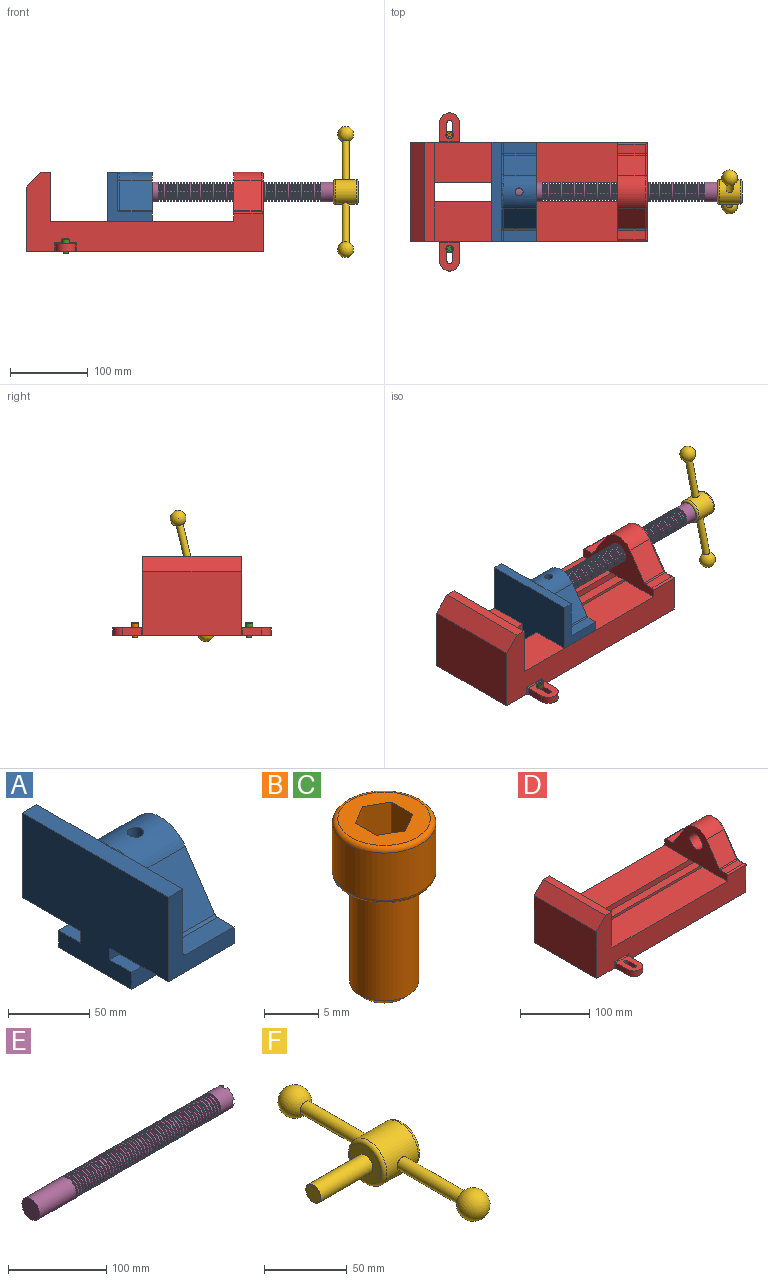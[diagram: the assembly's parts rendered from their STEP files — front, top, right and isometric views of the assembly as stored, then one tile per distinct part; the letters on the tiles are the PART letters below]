
ASSEMBLY  parts=6 mates=6
PART A: 36 faces, bbox 57.2x127x89 mm
  f0: plane 57.15x50.8mm, normal (0,0,-1), area 2903.2mm2, adj f6,f9,f10,f23
  f1: cylinder r=12.7mm len=44.45mm, axis (1,0,0), area 3464.3mm2, adj f6,f15,f16
  f2: plane 41.91x14.52mm, normal (0,0,1), area 608.5mm2, adj f6,f11,f24,f25
  f3: plane 51.86x48.26mm, normal (1,0,0), area 1495.7mm2, adj f8,f10,f31,f33,f35
  f4: plane 51.86x48.26mm, normal (1,0,0), area 1495.7mm2, adj f8,f11,f24,f28,f29
  f5: plane 57.15x50.8mm, normal (0,0,-1), area 2903.2mm2, adj f6,f9,f11,f22
  f6: plane 127x85.09mm, normal (1,0,0), area 5190.6mm2, adj f0,f1,f2,f5,f7,f10,f11,f12
  f7: plane 41.91x14.52mm, normal (0,0,1), area 608.5mm2, adj f6,f10,f30,f31
  f8: plane 127x12.7mm, normal (0,0,1), area 1612.9mm2, adj f3,f4,f9,f10,f11,f26,f34
  f9: plane 127x85.09mm, normal (-1,0,0), area 9096.8mm2, adj f0,f5,f8,f10,f11,f17,f18,f19
  f10: plane 63.5x57.15mm, normal (0,-1,0), area 1372.3mm2, adj f0,f3,f6,f7,f8,f9,f31
  f11: plane 63.5x57.15mm, normal (0,1,0), area 1372.3mm2, adj f2,f4,f5,f6,f8,f9,f24
  f12: plane 41.91x38.43mm, normal (0,-0.83,0.56), area 1939.2mm2, adj f6,f13,f30,f33
  f13: cylinder r=25.4mm len=44.45mm, axis (1,0,0), area 2026.5mm2, adj f6,f12,f14,f16,f26,f28,f34,f35
  f14: plane 41.91x38.43mm, normal (0,0.83,0.56), area 1939.2mm2, adj f6,f13,f25,f29
  f15: plane 25.4x25.4mm, normal (1,0,0), area 506.7mm2, adj f1
  f16: cylinder r=5.08mm len=13.76mm, axis (0,0,1), area 414mm2, adj f1,f13
  f17: plane 57.15x19.05mm, normal (0,0,1), area 1088.7mm2, adj f6,f9,f18,f23
  f18: plane 57.15x12.7mm, normal (0,-1,0), area 725.8mm2, adj f6,f9,f17,f19
  f19: plane 63.5x57.15mm, normal (0,0,-1), area 3629mm2, adj f6,f9,f18,f20
  f20: plane 57.15x12.7mm, normal (0,1,0), area 725.8mm2, adj f6,f9,f19,f21
  f21: plane 57.15x19.05mm, normal (0,0,1), area 1088.7mm2, adj f6,f9,f20,f22
  f22: plane 57.15x8.89mm, normal (0,1,0), area 508.1mm2, adj f5,f6,f9,f21
  f23: plane 57.15x8.89mm, normal (0,-1,0), area 508.1mm2, adj f0,f6,f9,f17
  f24: cylinder r=2.54mm len=14.52mm, axis (0,-1,0), area 57.9mm2, adj f2,f4,f11,f27
  f25: cylinder r=2.54mm len=41.91mm, axis (1,0,0), area 104.3mm2, adj f2,f6,f14,f27
  f26: bspline ~12.24x2.8mm, area 20.9mm2, adj f8,f13,f28
  f27: sphere r=2.54mm, area 6.3mm2, adj f24,f25,f29
  f28: torus R=27.94mm, axis (1,0,0), area 57.8mm2, adj f4,f13,f26,f29
  f29: cylinder r=2.54mm len=39.84mm, axis (0,-0.56,0.83), area 184.6mm2, adj f4,f14,f27,f28
  f30: cylinder r=2.54mm len=41.91mm, axis (1,0,0), area 104.3mm2, adj f6,f7,f12,f32
  f31: cylinder r=2.54mm len=14.52mm, axis (0,-1,0), area 57.9mm2, adj f3,f7,f10,f32
  f32: sphere r=2.54mm, area 6.3mm2, adj f30,f31,f33
  f33: cylinder r=2.54mm len=39.84mm, axis (0,-0.56,-0.83), area 184.6mm2, adj f3,f12,f32,f35
  f34: bspline ~12.24x2.8mm, area 20.9mm2, adj f8,f13,f35
  f35: torus R=27.94mm, axis (1,0,0), area 57.8mm2, adj f3,f13,f33,f34
PART B: 15 faces, bbox 10.3x10.3x19.1 mm
  f0: plane 8.51x8.51mm, normal (0,0,1), area 37.2mm2, adj f5,f6,f7,f8,f9,f10,f14
  f1: cylinder r=3.17mm len=11.94mm, axis (0,0,1), area 238.2mm2, adj f4,f12
  f2: plane 4.83x4.83mm, normal (0,0,-1), area 18.3mm2, adj f12
  f3: cylinder r=4.76mm len=9.53mm, axis (0,0,-1), area 159.6mm2, adj f13,f14
  f4: plane 8.51x8.51mm, normal (0,0,-1), area 25.2mm2, adj f1,f13
  f5: plane 4.83x2.38mm, normal (-0.5,-0.87,0), area 13.3mm2, adj f0,f6,f10,f11
  f6: plane 4.83x2.38mm, normal (0.5,-0.87,0), area 13.3mm2, adj f0,f5,f7,f11
  f7: plane 4.83x2.75mm, normal (1,0,0), area 13.3mm2, adj f0,f6,f8,f11
  f8: plane 4.83x2.38mm, normal (0.5,0.87,0), area 13.3mm2, adj f0,f7,f9,f11
  f9: plane 4.83x2.38mm, normal (-0.5,0.87,0), area 13.3mm2, adj f0,f8,f10,f11
  f10: plane 4.83x2.75mm, normal (-1,0,0), area 13.3mm2, adj f0,f5,f9,f11
  f11: plane 5.5x4.76mm, normal (0,0,1), area 19.6mm2, adj f5,f6,f7,f8,f9,f10
  f12: cone r=3.17mm half-angle=45deg, axis (0,0,1), area 18.9mm2, adj f1,f2
  f13: torus R=4.25mm, axis (0,0,1), area 23mm2, adj f3,f4
  f14: torus R=4.25mm, axis (0,0,1), area 23mm2, adj f0,f3
PART C: same geometry as B
PART D: 61 faces, bbox 304.8x203.2x103.7 mm
  f0: plane 304.8x101.6mm, normal (0,1,0), area 13520.3mm2, adj f3,f4,f5,f6,f7,f8,f9,f16
  f1: plane 304.8x101.6mm, normal (0,-1,0), area 13520.3mm2, adj f2,f3,f5,f6,f7,f8,f9,f16
  f2: plane 234.95x50.8mm, normal (0,0,1), area 11935.5mm2, adj f1,f5,f16,f26
  f3: plane 127x99.06mm, normal (1,0,0), area 7097.5mm2, adj f0,f1,f9,f14,f17,f18,f19,f20
  f4: plane 234.95x50.8mm, normal (0,0,1), area 11935.5mm2, adj f0,f5,f16,f27
  f5: plane 127x101.6mm, normal (1,0,0), area 9516.1mm2, adj f0,f1,f2,f4,f6,f9,f18,f19
  f6: plane 127x12.7mm, normal (0,0,1), area 1612.9mm2, adj f0,f1,f5,f7
  f7: plane 127x19.05mm, normal (-0.71,0,0.71), area 3421.5mm2, adj f0,f1,f6,f8
  f8: plane 127x82.55mm, normal (-1,0,0), area 10483.8mm2, adj f0,f1,f7,f9
  f9: plane 304.8x203.2mm, normal (0,0,-1), area 33298.3mm2, adj f0,f1,f3,f5,f8,f21,f22,f39
  f10: plane 35.56x11.98mm, normal (0,0,1), area 426mm2, adj f16,f28,f29,f30
  f11: plane 38.43x35.56mm, normal (0,0.83,0.56), area 1645.4mm2, adj f12,f16,f29,f32
  f12: cylinder r=25.4mm len=42.19mm, axis (1,0,0), area 1770.2mm2, adj f11,f13,f16,f33
  f13: plane 38.43x35.56mm, normal (0,-0.83,0.56), area 1645.4mm2, adj f12,f16,f34,f35
  f14: cylinder r=12.7mm len=38.1mm, axis (1,0,0), area 3040.2mm2, adj f3,f16
  f15: plane 35.56x11.98mm, normal (0,0,1), area 426mm2, adj f16,f34,f36,f38
  f16: plane 127x63.5mm, normal (-1,0,0), area 4155.5mm2, adj f0,f1,f2,f4,f10,f11,f12,f13
  f17: plane 38.1x25.4mm, normal (0,0,-1), area 967.7mm2, adj f3,f16,f26,f27
  f18: plane 273.05x19.05mm, normal (0,0,-1), area 5201.6mm2, adj f3,f5,f19,f26
  f19: plane 273.05x12.7mm, normal (0,1,0), area 3467.7mm2, adj f3,f5,f18,f20
  f20: plane 273.05x19.05mm, normal (0,0,1), area 5201.6mm2, adj f3,f5,f19,f21
  f21: plane 273.05x16.51mm, normal (0,1,0), area 4508.1mm2, adj f3,f5,f9,f20
  f22: plane 273.05x16.51mm, normal (0,-1,0), area 4508.1mm2, adj f3,f5,f9,f23
  f23: plane 273.05x19.05mm, normal (0,0,1), area 5201.6mm2, adj f3,f5,f22,f24
  f24: plane 273.05x12.7mm, normal (0,-1,0), area 3467.7mm2, adj f3,f5,f23,f25
  f25: plane 273.05x19.05mm, normal (0,0,-1), area 5201.6mm2, adj f3,f5,f24,f27
  f26: plane 273.05x8.89mm, normal (0,1,0), area 2427.4mm2, adj f2,f3,f5,f17,f18
  f27: plane 273.05x8.89mm, normal (0,-1,0), area 2427.4mm2, adj f3,f4,f5,f17,f25
  f28: cylinder r=2.54mm len=38.1mm, axis (1,0,0), area 148.3mm2, adj f0,f10,f16,f30
  f29: cylinder r=2.54mm len=35.56mm, axis (-1,0,0), area 88.5mm2, adj f10,f11,f16,f31
  f30: cylinder r=2.54mm len=14.52mm, axis (0,1,0), area 54.3mm2, adj f3,f10,f28,f31
  f31: torus R=5.08mm, axis (-1,0,0), area 13.5mm2, adj f3,f29,f30,f32
  f32: cylinder r=2.54mm len=39.84mm, axis (0,0.56,-0.83), area 184.6mm2, adj f3,f11,f31,f33
  f33: torus R=22.86mm, axis (-1,0,0), area 191.4mm2, adj f3,f12,f32,f35
  f34: cylinder r=2.54mm len=35.56mm, axis (-1,0,0), area 88.5mm2, adj f13,f15,f16,f37
  f35: cylinder r=2.54mm len=39.84mm, axis (0,0.56,0.83), area 184.6mm2, adj f3,f13,f33,f37
  f36: cylinder r=2.54mm len=38.1mm, axis (-1,0,0), area 148.3mm2, adj f1,f15,f16,f38
  f37: torus R=5.08mm, axis (-1,0,0), area 13.5mm2, adj f3,f34,f35,f38
  f38: cylinder r=2.54mm len=14.52mm, axis (0,1,0), area 54.3mm2, adj f3,f15,f36,f37
  f39: plane 23.88x9.53mm, normal (-1,0,0), area 227.4mm2, adj f9,f45,f46,f60
  f40: plane 23.88x9.53mm, normal (1,0,0), area 227.4mm2, adj f9,f45,f46,f58
  f41: cylinder r=3.3mm len=9.53mm, axis (0,0,-1), area 98.8mm2, adj f9,f42,f44,f46
  f42: plane 15.62x9.53mm, normal (-1,0,0), area 148.8mm2, adj f9,f41,f43,f46
  f43: cylinder r=3.3mm len=9.53mm, axis (0,0,-1), area 98.8mm2, adj f9,f42,f44,f46
  f44: plane 15.62x9.53mm, normal (1,0,0), area 148.8mm2, adj f9,f41,f43,f46
  f45: cylinder r=12.7mm len=25.4mm, axis (0,0,-1), area 380mm2, adj f9,f39,f40,f46
  f46: plane 36.58x25.4mm, normal (0,0,1), area 722.4mm2, adj f39,f40,f41,f42,f43,f44,f45,f59
  f47: plane 23.88x9.53mm, normal (-1,0,0), area 227.4mm2, adj f9,f53,f54,f56
  f48: plane 23.88x9.53mm, normal (1,0,0), area 227.4mm2, adj f9,f53,f54,f55
  f49: cylinder r=3.3mm len=9.53mm, axis (0,0,-1), area 98.8mm2, adj f9,f50,f52,f54
  f50: plane 15.62x9.53mm, normal (-1,0,0), area 148.8mm2, adj f9,f49,f51,f54
  f51: cylinder r=3.3mm len=9.53mm, axis (0,0,-1), area 98.8mm2, adj f9,f50,f52,f54
  f52: plane 15.62x9.53mm, normal (1,0,0), area 148.8mm2, adj f9,f49,f51,f54
  f53: cylinder r=12.7mm len=25.4mm, axis (0,0,-1), area 380mm2, adj f9,f47,f48,f54
  f54: plane 36.58x25.4mm, normal (0,0,1), area 722.4mm2, adj f47,f48,f49,f50,f51,f52,f53,f57
  f55: cylinder r=1.52mm len=11.05mm, axis (0,0,-1), area 24.1mm2, adj f0,f9,f48,f57
  f56: cylinder r=1.52mm len=11.05mm, axis (0,0,1), area 24.1mm2, adj f0,f9,f47,f57
  f57: cylinder r=1.52mm len=28.45mm, axis (1,0,0), area 63.5mm2, adj f0,f54,f55,f56
  f58: cylinder r=1.52mm len=11.05mm, axis (0,0,1), area 24.1mm2, adj f1,f9,f40,f59
  f59: cylinder r=1.52mm len=28.45mm, axis (-1,0,0), area 63.5mm2, adj f1,f46,f58,f60
  f60: cylinder r=1.52mm len=11.05mm, axis (0,0,-1), area 24.1mm2, adj f1,f9,f39,f59
PART E: 220 faces, bbox 279.4x25.4x25.4 mm
  f0: cylinder r=12.7mm len=25.4mm, axis (-1,0,0), area 1468.2mm2, adj f1,f2,f3,f5,f7,f208,f209,f210
  f1: plane 9.9x9.9mm, normal (1,0,0), area 62.3mm2, adj f0,f4,f213,f216
  f2: plane 9.9x9.9mm, normal (1,0,0), area 62.3mm2, adj f0,f4,f210,f218
  f3: plane 9.9x9.9mm, normal (1,0,0), area 62.3mm2, adj f0,f4,f209,f212
  f4: cylinder r=6.35mm len=25.4mm, axis (1,0,0), area 960.3mm2, adj f1,f2,f3,f5,f6,f208,f209,f210
  f5: plane 9.9x9.9mm, normal (1,0,0), area 62.3mm2, adj f0,f4,f215,f217
  f6: plane 12.7x12.7mm, normal (1,0,0), area 126.7mm2, adj f4
  f7: cone r=12.7mm half-angle=76deg, axis (1,0,0), area 188mm2, adj f0,f9
  f8: cone r=10.16mm half-angle=76deg, axis (-1,0,0), area 188mm2, adj f9,f10
  f9: cylinder r=10.16mm len=20.32mm, axis (1,0,0), area 81.1mm2, adj f7,f8
  f10: cylinder r=12.7mm len=25.4mm, axis (-1,0,0), area 131.7mm2, adj f8,f11
  f11: cone r=12.7mm half-angle=76deg, axis (1,0,0), area 188mm2, adj f10,f13
  f12: cone r=10.16mm half-angle=76deg, axis (-1,0,0), area 188mm2, adj f13,f14
  f13: cylinder r=10.16mm len=20.32mm, axis (1,0,0), area 81.1mm2, adj f11,f12
  f14: cylinder r=12.7mm len=25.4mm, axis (-1,0,0), area 131.7mm2, adj f12,f15
  f15: cone r=12.7mm half-angle=76deg, axis (1,0,0), area 188mm2, adj f14,f17
  f16: cone r=10.16mm half-angle=76deg, axis (-1,0,0), area 188mm2, adj f17,f18
  f17: cylinder r=10.16mm len=20.32mm, axis (1,0,0), area 81.1mm2, adj f15,f16
  f18: cylinder r=12.7mm len=25.4mm, axis (-1,0,0), area 131.7mm2, adj f16,f19
  f19: cone r=12.7mm half-angle=76deg, axis (1,0,0), area 188mm2, adj f18,f21
  f20: cone r=10.16mm half-angle=76deg, axis (-1,0,0), area 188mm2, adj f21,f22
  f21: cylinder r=10.16mm len=20.32mm, axis (1,0,0), area 81.1mm2, adj f19,f20
  f22: cylinder r=12.7mm len=25.4mm, axis (-1,0,0), area 131.7mm2, adj f20,f23
  f23: cone r=12.7mm half-angle=76deg, axis (1,0,0), area 188mm2, adj f22,f25
  f24: cone r=10.16mm half-angle=76deg, axis (-1,0,0), area 188mm2, adj f25,f26
  f25: cylinder r=10.16mm len=20.32mm, axis (1,0,0), area 81.1mm2, adj f23,f24
  f26: cylinder r=12.7mm len=25.4mm, axis (-1,0,0), area 131.7mm2, adj f24,f27
  f27: cone r=12.7mm half-angle=76deg, axis (1,0,0), area 188mm2, adj f26,f29
  f28: cone r=10.16mm half-angle=76deg, axis (-1,0,0), area 188mm2, adj f29,f30
  f29: cylinder r=10.16mm len=20.32mm, axis (1,0,0), area 81.1mm2, adj f27,f28
  f30: cylinder r=12.7mm len=25.4mm, axis (-1,0,0), area 131.7mm2, adj f28,f31
  f31: cone r=12.7mm half-angle=76deg, axis (1,0,0), area 188mm2, adj f30,f33
  f32: cone r=10.16mm half-angle=76deg, axis (-1,0,0), area 188mm2, adj f33,f34
  f33: cylinder r=10.16mm len=20.32mm, axis (1,0,0), area 81.1mm2, adj f31,f32
  f34: cylinder r=12.7mm len=25.4mm, axis (-1,0,0), area 131.7mm2, adj f32,f35
  f35: cone r=12.7mm half-angle=76deg, axis (1,0,0), area 188mm2, adj f34,f37
  f36: cone r=10.16mm half-angle=76deg, axis (-1,0,0), area 188mm2, adj f37,f38
  f37: cylinder r=10.16mm len=20.32mm, axis (1,0,0), area 81.1mm2, adj f35,f36
  f38: cylinder r=12.7mm len=25.4mm, axis (-1,0,0), area 131.7mm2, adj f36,f39
  f39: cone r=12.7mm half-angle=76deg, axis (1,0,0), area 188mm2, adj f38,f41
  f40: cone r=10.16mm half-angle=76deg, axis (-1,0,0), area 188mm2, adj f41,f42
  f41: cylinder r=10.16mm len=20.32mm, axis (1,0,0), area 81.1mm2, adj f39,f40
  f42: cylinder r=12.7mm len=25.4mm, axis (-1,0,0), area 131.7mm2, adj f40,f43
  f43: cone r=12.7mm half-angle=76deg, axis (1,0,0), area 188mm2, adj f42,f45
  f44: cone r=10.16mm half-angle=76deg, axis (-1,0,0), area 188mm2, adj f45,f46
  f45: cylinder r=10.16mm len=20.32mm, axis (1,0,0), area 81.1mm2, adj f43,f44
  f46: cylinder r=12.7mm len=25.4mm, axis (-1,0,0), area 131.7mm2, adj f44,f47
  f47: cone r=12.7mm half-angle=76deg, axis (1,0,0), area 188mm2, adj f46,f49
  f48: cone r=10.16mm half-angle=76deg, axis (-1,0,0), area 188mm2, adj f49,f50
  f49: cylinder r=10.16mm len=20.32mm, axis (1,0,0), area 81.1mm2, adj f47,f48
  f50: cylinder r=12.7mm len=25.4mm, axis (-1,0,0), area 131.7mm2, adj f48,f51
  f51: cone r=12.7mm half-angle=76deg, axis (1,0,0), area 188mm2, adj f50,f53
  f52: cone r=10.16mm half-angle=76deg, axis (-1,0,0), area 188mm2, adj f53,f54
  f53: cylinder r=10.16mm len=20.32mm, axis (1,0,0), area 81.1mm2, adj f51,f52
  f54: cylinder r=12.7mm len=25.4mm, axis (-1,0,0), area 131.7mm2, adj f52,f55
  f55: cone r=12.7mm half-angle=76deg, axis (1,0,0), area 188mm2, adj f54,f57
  f56: cone r=10.16mm half-angle=76deg, axis (-1,0,0), area 188mm2, adj f57,f58
  f57: cylinder r=10.16mm len=20.32mm, axis (1,0,0), area 81.1mm2, adj f55,f56
  f58: cylinder r=12.7mm len=25.4mm, axis (-1,0,0), area 131.7mm2, adj f56,f59
  f59: cone r=12.7mm half-angle=76deg, axis (1,0,0), area 188mm2, adj f58,f61
  f60: cone r=10.16mm half-angle=76deg, axis (-1,0,0), area 188mm2, adj f61,f62
  f61: cylinder r=10.16mm len=20.32mm, axis (1,0,0), area 81.1mm2, adj f59,f60
  f62: cylinder r=12.7mm len=25.4mm, axis (-1,0,0), area 131.7mm2, adj f60,f63
  f63: cone r=12.7mm half-angle=76deg, axis (1,0,0), area 188mm2, adj f62,f65
  f64: cone r=10.16mm half-angle=76deg, axis (-1,0,0), area 188mm2, adj f65,f66
  f65: cylinder r=10.16mm len=20.32mm, axis (1,0,0), area 81.1mm2, adj f63,f64
  f66: cylinder r=12.7mm len=25.4mm, axis (-1,0,0), area 131.7mm2, adj f64,f67
  f67: cone r=12.7mm half-angle=76deg, axis (1,0,0), area 188mm2, adj f66,f69
  f68: cone r=10.16mm half-angle=76deg, axis (-1,0,0), area 188mm2, adj f69,f70
  f69: cylinder r=10.16mm len=20.32mm, axis (1,0,0), area 81.1mm2, adj f67,f68
  f70: cylinder r=12.7mm len=25.4mm, axis (-1,0,0), area 131.7mm2, adj f68,f71
  f71: cone r=12.7mm half-angle=76deg, axis (1,0,0), area 188mm2, adj f70,f73
  f72: cone r=10.16mm half-angle=76deg, axis (-1,0,0), area 188mm2, adj f73,f74
  f73: cylinder r=10.16mm len=20.32mm, axis (1,0,0), area 81.1mm2, adj f71,f72
  f74: cylinder r=12.7mm len=25.4mm, axis (-1,0,0), area 131.7mm2, adj f72,f75
  f75: cone r=12.7mm half-angle=76deg, axis (1,0,0), area 188mm2, adj f74,f77
  f76: cone r=10.16mm half-angle=76deg, axis (-1,0,0), area 188mm2, adj f77,f78
  f77: cylinder r=10.16mm len=20.32mm, axis (1,0,0), area 81.1mm2, adj f75,f76
  f78: cylinder r=12.7mm len=25.4mm, axis (-1,0,0), area 131.7mm2, adj f76,f79
  f79: cone r=12.7mm half-angle=76deg, axis (1,0,0), area 188mm2, adj f78,f81
  f80: cone r=10.16mm half-angle=76deg, axis (-1,0,0), area 188mm2, adj f81,f82
  f81: cylinder r=10.16mm len=20.32mm, axis (1,0,0), area 81.1mm2, adj f79,f80
  f82: cylinder r=12.7mm len=25.4mm, axis (-1,0,0), area 131.7mm2, adj f80,f83
  f83: cone r=12.7mm half-angle=76deg, axis (1,0,0), area 188mm2, adj f82,f85
  f84: cone r=10.16mm half-angle=76deg, axis (-1,0,0), area 188mm2, adj f85,f86
  f85: cylinder r=10.16mm len=20.32mm, axis (1,0,0), area 81.1mm2, adj f83,f84
  f86: cylinder r=12.7mm len=25.4mm, axis (-1,0,0), area 131.7mm2, adj f84,f87
  f87: cone r=12.7mm half-angle=76deg, axis (1,0,0), area 188mm2, adj f86,f89
  f88: cone r=10.16mm half-angle=76deg, axis (-1,0,0), area 188mm2, adj f89,f90
  f89: cylinder r=10.16mm len=20.32mm, axis (1,0,0), area 81.1mm2, adj f87,f88
  f90: cylinder r=12.7mm len=25.4mm, axis (-1,0,0), area 131.7mm2, adj f88,f91
  f91: cone r=12.7mm half-angle=76deg, axis (1,0,0), area 188mm2, adj f90,f93
  f92: cone r=10.16mm half-angle=76deg, axis (-1,0,0), area 188mm2, adj f93,f94
  f93: cylinder r=10.16mm len=20.32mm, axis (1,0,0), area 81.1mm2, adj f91,f92
  f94: cylinder r=12.7mm len=25.4mm, axis (-1,0,0), area 131.7mm2, adj f92,f95
  f95: cone r=12.7mm half-angle=76deg, axis (1,0,0), area 188mm2, adj f94,f97
  f96: cone r=10.16mm half-angle=76deg, axis (-1,0,0), area 188mm2, adj f97,f98
  f97: cylinder r=10.16mm len=20.32mm, axis (1,0,0), area 81.1mm2, adj f95,f96
  f98: cylinder r=12.7mm len=25.4mm, axis (-1,0,0), area 131.7mm2, adj f96,f99
  f99: cone r=12.7mm half-angle=76deg, axis (1,0,0), area 188mm2, adj f98,f101
  f100: cone r=10.16mm half-angle=76deg, axis (-1,0,0), area 188mm2, adj f101,f102
  f101: cylinder r=10.16mm len=20.32mm, axis (1,0,0), area 81.1mm2, adj f99,f100
  f102: cylinder r=12.7mm len=25.4mm, axis (-1,0,0), area 131.7mm2, adj f100,f103
  f103: cone r=12.7mm half-angle=76deg, axis (1,0,0), area 188mm2, adj f102,f105
  f104: cone r=10.16mm half-angle=76deg, axis (-1,0,0), area 188mm2, adj f105,f106
  f105: cylinder r=10.16mm len=20.32mm, axis (1,0,0), area 81.1mm2, adj f103,f104
  f106: cylinder r=12.7mm len=25.4mm, axis (-1,0,0), area 131.7mm2, adj f104,f107
  f107: cone r=12.7mm half-angle=76deg, axis (1,0,0), area 188mm2, adj f106,f109
  f108: cone r=10.16mm half-angle=76deg, axis (-1,0,0), area 188mm2, adj f109,f110
  f109: cylinder r=10.16mm len=20.32mm, axis (1,0,0), area 81.1mm2, adj f107,f108
  f110: cylinder r=12.7mm len=25.4mm, axis (-1,0,0), area 131.7mm2, adj f108,f111
  f111: cone r=12.7mm half-angle=76deg, axis (1,0,0), area 188mm2, adj f110,f113
  f112: cone r=10.16mm half-angle=76deg, axis (-1,0,0), area 188mm2, adj f113,f114
  f113: cylinder r=10.16mm len=20.32mm, axis (1,0,0), area 81.1mm2, adj f111,f112
  f114: cylinder r=12.7mm len=25.4mm, axis (-1,0,0), area 131.7mm2, adj f112,f115
  f115: cone r=12.7mm half-angle=76deg, axis (1,0,0), area 188mm2, adj f114,f117
  f116: cone r=10.16mm half-angle=76deg, axis (-1,0,0), area 188mm2, adj f117,f118
  f117: cylinder r=10.16mm len=20.32mm, axis (1,0,0), area 81.1mm2, adj f115,f116
  f118: cylinder r=12.7mm len=25.4mm, axis (-1,0,0), area 131.7mm2, adj f116,f119
  f119: cone r=12.7mm half-angle=76deg, axis (1,0,0), area 188mm2, adj f118,f121
  f120: cone r=10.16mm half-angle=76deg, axis (-1,0,0), area 188mm2, adj f121,f122
  f121: cylinder r=10.16mm len=20.32mm, axis (1,0,0), area 81.1mm2, adj f119,f120
  f122: cylinder r=12.7mm len=25.4mm, axis (-1,0,0), area 131.7mm2, adj f120,f123
  f123: cone r=12.7mm half-angle=76deg, axis (1,0,0), area 188mm2, adj f122,f125
  f124: cone r=10.16mm half-angle=76deg, axis (-1,0,0), area 188mm2, adj f125,f126
  f125: cylinder r=10.16mm len=20.32mm, axis (1,0,0), area 81.1mm2, adj f123,f124
  f126: cylinder r=12.7mm len=25.4mm, axis (-1,0,0), area 131.7mm2, adj f124,f127
  f127: cone r=12.7mm half-angle=76deg, axis (1,0,0), area 188mm2, adj f126,f129
  f128: cone r=10.16mm half-angle=76deg, axis (-1,0,0), area 188mm2, adj f129,f130
  f129: cylinder r=10.16mm len=20.32mm, axis (1,0,0), area 81.1mm2, adj f127,f128
  f130: cylinder r=12.7mm len=25.4mm, axis (-1,0,0), area 131.7mm2, adj f128,f131
  f131: cone r=12.7mm half-angle=76deg, axis (1,0,0), area 188mm2, adj f130,f133
  f132: cone r=10.16mm half-angle=76deg, axis (-1,0,0), area 188mm2, adj f133,f134
  f133: cylinder r=10.16mm len=20.32mm, axis (1,0,0), area 81.1mm2, adj f131,f132
  f134: cylinder r=12.7mm len=25.4mm, axis (-1,0,0), area 131.7mm2, adj f132,f135
  f135: cone r=12.7mm half-angle=76deg, axis (1,0,0), area 188mm2, adj f134,f137
  f136: cone r=10.16mm half-angle=76deg, axis (-1,0,0), area 188mm2, adj f137,f138
  f137: cylinder r=10.16mm len=20.32mm, axis (1,0,0), area 81.1mm2, adj f135,f136
  f138: cylinder r=12.7mm len=25.4mm, axis (-1,0,0), area 131.7mm2, adj f136,f139
  f139: cone r=12.7mm half-angle=76deg, axis (1,0,0), area 188mm2, adj f138,f141
  f140: cone r=10.16mm half-angle=76deg, axis (-1,0,0), area 188mm2, adj f141,f142
  f141: cylinder r=10.16mm len=20.32mm, axis (1,0,0), area 81.1mm2, adj f139,f140
  f142: cylinder r=12.7mm len=25.4mm, axis (-1,0,0), area 131.7mm2, adj f140,f143
  f143: cone r=12.7mm half-angle=76deg, axis (1,0,0), area 188mm2, adj f142,f145
  f144: cone r=10.16mm half-angle=76deg, axis (-1,0,0), area 188mm2, adj f145,f146
  f145: cylinder r=10.16mm len=20.32mm, axis (1,0,0), area 81.1mm2, adj f143,f144
  f146: cylinder r=12.7mm len=25.4mm, axis (-1,0,0), area 131.7mm2, adj f144,f147
  f147: cone r=12.7mm half-angle=76deg, axis (1,0,0), area 188mm2, adj f146,f149
  f148: cone r=10.16mm half-angle=76deg, axis (-1,0,0), area 188mm2, adj f149,f150
  f149: cylinder r=10.16mm len=20.32mm, axis (1,0,0), area 81.1mm2, adj f147,f148
  f150: cylinder r=12.7mm len=25.4mm, axis (-1,0,0), area 131.7mm2, adj f148,f151
  f151: cone r=12.7mm half-angle=76deg, axis (1,0,0), area 188mm2, adj f150,f153
  f152: cone r=10.16mm half-angle=76deg, axis (-1,0,0), area 188mm2, adj f153,f154
  f153: cylinder r=10.16mm len=20.32mm, axis (1,0,0), area 81.1mm2, adj f151,f152
  f154: cylinder r=12.7mm len=25.4mm, axis (-1,0,0), area 131.7mm2, adj f152,f155
  f155: cone r=12.7mm half-angle=76deg, axis (1,0,0), area 188mm2, adj f154,f157
  f156: cone r=10.16mm half-angle=76deg, axis (-1,0,0), area 188mm2, adj f157,f158
  f157: cylinder r=10.16mm len=20.32mm, axis (1,0,0), area 81.1mm2, adj f155,f156
  f158: cylinder r=12.7mm len=25.4mm, axis (-1,0,0), area 131.7mm2, adj f156,f159
  f159: cone r=12.7mm half-angle=76deg, axis (1,0,0), area 188mm2, adj f158,f161
  f160: cone r=10.16mm half-angle=76deg, axis (-1,0,0), area 188mm2, adj f161,f162
  f161: cylinder r=10.16mm len=20.32mm, axis (1,0,0), area 81.1mm2, adj f159,f160
  f162: cylinder r=12.7mm len=25.4mm, axis (-1,0,0), area 131.7mm2, adj f160,f163
  f163: cone r=12.7mm half-angle=76deg, axis (1,0,0), area 188mm2, adj f162,f165
  f164: cone r=10.16mm half-angle=76deg, axis (-1,0,0), area 188mm2, adj f165,f166
  f165: cylinder r=10.16mm len=20.32mm, axis (1,0,0), area 81.1mm2, adj f163,f164
  f166: cylinder r=12.7mm len=25.4mm, axis (-1,0,0), area 131.7mm2, adj f164,f167
  f167: cone r=12.7mm half-angle=76deg, axis (1,0,0), area 188mm2, adj f166,f169
  f168: cone r=10.16mm half-angle=76deg, axis (-1,0,0), area 188mm2, adj f169,f170
  f169: cylinder r=10.16mm len=20.32mm, axis (1,0,0), area 81.1mm2, adj f167,f168
  f170: cylinder r=12.7mm len=25.4mm, axis (-1,0,0), area 131.7mm2, adj f168,f171
  f171: cone r=12.7mm half-angle=76deg, axis (1,0,0), area 188mm2, adj f170,f173
  f172: cone r=10.16mm half-angle=76deg, axis (-1,0,0), area 188mm2, adj f173,f174
  f173: cylinder r=10.16mm len=20.32mm, axis (1,0,0), area 81.1mm2, adj f171,f172
  f174: cylinder r=12.7mm len=25.4mm, axis (-1,0,0), area 131.7mm2, adj f172,f175
  f175: cone r=12.7mm half-angle=76deg, axis (1,0,0), area 188mm2, adj f174,f177
  f176: cone r=10.16mm half-angle=76deg, axis (-1,0,0), area 188mm2, adj f177,f178
  f177: cylinder r=10.16mm len=20.32mm, axis (1,0,0), area 81.1mm2, adj f175,f176
  f178: cylinder r=12.7mm len=25.4mm, axis (-1,0,0), area 131.7mm2, adj f176,f179
  f179: cone r=12.7mm half-angle=76deg, axis (1,0,0), area 188mm2, adj f178,f181
  f180: cone r=10.16mm half-angle=76deg, axis (-1,0,0), area 188mm2, adj f181,f182
  f181: cylinder r=10.16mm len=20.32mm, axis (1,0,0), area 81.1mm2, adj f179,f180
  f182: cylinder r=12.7mm len=25.4mm, axis (-1,0,0), area 131.7mm2, adj f180,f183
  f183: cone r=12.7mm half-angle=76deg, axis (1,0,0), area 188mm2, adj f182,f185
  f184: cone r=10.16mm half-angle=76deg, axis (-1,0,0), area 188mm2, adj f185,f186
  f185: cylinder r=10.16mm len=20.32mm, axis (1,0,0), area 81.1mm2, adj f183,f184
  f186: cylinder r=12.7mm len=25.4mm, axis (-1,0,0), area 131.7mm2, adj f184,f187
  f187: cone r=12.7mm half-angle=76deg, axis (1,0,0), area 188mm2, adj f186,f189
  f188: cone r=10.16mm half-angle=76deg, axis (-1,0,0), area 188mm2, adj f189,f190
  f189: cylinder r=10.16mm len=20.32mm, axis (1,0,0), area 81.1mm2, adj f187,f188
  f190: cylinder r=12.7mm len=25.4mm, axis (-1,0,0), area 131.7mm2, adj f188,f191
  f191: cone r=12.7mm half-angle=76deg, axis (1,0,0), area 188mm2, adj f190,f193
  f192: cone r=10.16mm half-angle=76deg, axis (-1,0,0), area 188mm2, adj f193,f194
  f193: cylinder r=10.16mm len=20.32mm, axis (1,0,0), area 81.1mm2, adj f191,f192
  f194: cylinder r=12.7mm len=25.4mm, axis (-1,0,0), area 131.7mm2, adj f192,f195
  f195: cone r=12.7mm half-angle=76deg, axis (1,0,0), area 188mm2, adj f194,f197
  f196: cone r=10.16mm half-angle=76deg, axis (-1,0,0), area 188mm2, adj f197,f198
  f197: cylinder r=10.16mm len=20.32mm, axis (1,0,0), area 81.1mm2, adj f195,f196
  f198: cylinder r=12.7mm len=25.4mm, axis (-1,0,0), area 131.7mm2, adj f196,f199
  f199: cone r=12.7mm half-angle=76deg, axis (1,0,0), area 188mm2, adj f198,f201
  f200: cone r=10.16mm half-angle=76deg, axis (-1,0,0), area 188mm2, adj f201,f202
  f201: cylinder r=10.16mm len=20.32mm, axis (1,0,0), area 81.1mm2, adj f199,f200
  f202: cylinder r=12.7mm len=25.4mm, axis (-1,0,0), area 131.7mm2, adj f200,f203
  f203: cone r=12.7mm half-angle=76deg, axis (1,0,0), area 188mm2, adj f202,f205
  f204: cone r=10.16mm half-angle=76deg, axis (-1,0,0), area 188mm2, adj f205,f207
  f205: cylinder r=10.16mm len=20.32mm, axis (1,0,0), area 81.1mm2, adj f203,f204
  f206: plane 25.4x25.4mm, normal (-1,0,0), area 506.7mm2, adj f207
  f207: cylinder r=12.7mm len=52.45mm, axis (-1,0,0), area 4185.4mm2, adj f204,f206
  f208: plane 6.88x5.08mm, normal (1,0,0), area 32.7mm2, adj f0,f4,f209,f210
  f209: plane 6.62x2.54mm, normal (0,-1,0), area 16.8mm2, adj f0,f3,f4,f208
  f210: plane 6.62x2.54mm, normal (0,1,0), area 16.8mm2, adj f0,f2,f4,f208
  f211: plane 6.88x5.08mm, normal (1,0,0), area 32.7mm2, adj f0,f4,f212,f213
  f212: plane 6.62x2.54mm, normal (0,0,1), area 16.8mm2, adj f0,f3,f4,f211
  f213: plane 6.62x2.54mm, normal (0,0,-1), area 16.8mm2, adj f0,f1,f4,f211
  f214: plane 6.88x5.08mm, normal (1,0,0), area 32.7mm2, adj f0,f4,f215,f216
  f215: plane 6.62x2.54mm, normal (0,1,0), area 16.8mm2, adj f0,f4,f5,f214
  f216: plane 6.62x2.54mm, normal (0,-1,0), area 16.8mm2, adj f0,f1,f4,f214
  f217: plane 6.62x2.54mm, normal (0,0,-1), area 16.8mm2, adj f0,f4,f5,f219
  f218: plane 6.62x2.54mm, normal (0,0,1), area 16.8mm2, adj f0,f2,f4,f219
  f219: plane 6.88x5.08mm, normal (1,0,0), area 32.7mm2, adj f0,f4,f217,f218
PART F: 11 faces, bbox 76.2x172.7x34.4 mm
  f0: sphere r=10.16mm, area 1231.8mm2, adj f1
  f1: cylinder r=4.45mm len=51.82mm, axis (0,1,0), area 1438.5mm2, adj f0,f4
  f2: sphere r=10.16mm, area 1231.8mm2, adj f3
  f3: cylinder r=4.45mm len=51.82mm, axis (0,1,0), area 1438.5mm2, adj f2,f4
  f4: cylinder r=15.88mm len=31.75mm, axis (-1,0,0), area 2534.7mm2, adj f1,f3,f9,f10
  f5: cylinder r=6.35mm len=44.45mm, axis (-1,0,0), area 1773.5mm2, adj f6,f8
  f6: plane 12.7x12.7mm, normal (-1,0,0), area 126.7mm2, adj f5
  f7: plane 26.67x26.67mm, normal (1,0,0), area 558.6mm2, adj f10
  f8: plane 26.67x26.67mm, normal (-1,0,0), area 432mm2, adj f5,f9
  f9: torus R=13.33mm, axis (1,0,0), area 374.8mm2, adj f4,f8
  f10: torus R=13.33mm, axis (1,0,0), area 374.8mm2, adj f4,f7
PLACE A t=(73.5,0,0)mm
PLACE B rot(axis=(0,0,1),102deg) t=(-254,73.28,9.53)mm
PLACE C rot(axis=(0,0,1),74.8deg) t=(-254,-73.28,9.52)mm
PLACE D at identity fixed
PLACE E rot(axis=(-1,0,0),103.6deg) t=(73.5,-74.07,94.07)mm
PLACE F rot(axis=(-1,0,0),103.6deg) t=(51.91,-74.07,94.07)mm
MATE pin_slot B.f1 <-> D.f51  axis (0,0,1) through (-254,73.28,9.52)mm
MATE fastened E.f4 <-> F.f5  axis (1,0,0) through (90.01,0,76.2)mm
MATE planar A.f0 <-> D.f2  axis (0,0,-1) through (-170.97,-38.1,38.1)mm
MATE pin_slot C.f1 <-> D.f41  axis (0,0,1) through (-254,-73.28,9.52)mm
MATE revolute E.f7 <-> A.f28  axis (-1,0,0) through (-186.85,0,76.2)mm
MATE cylindrical D.f12 <-> E.f7  axis (-1,0,0) through (-38.1,0,76.2)mm
